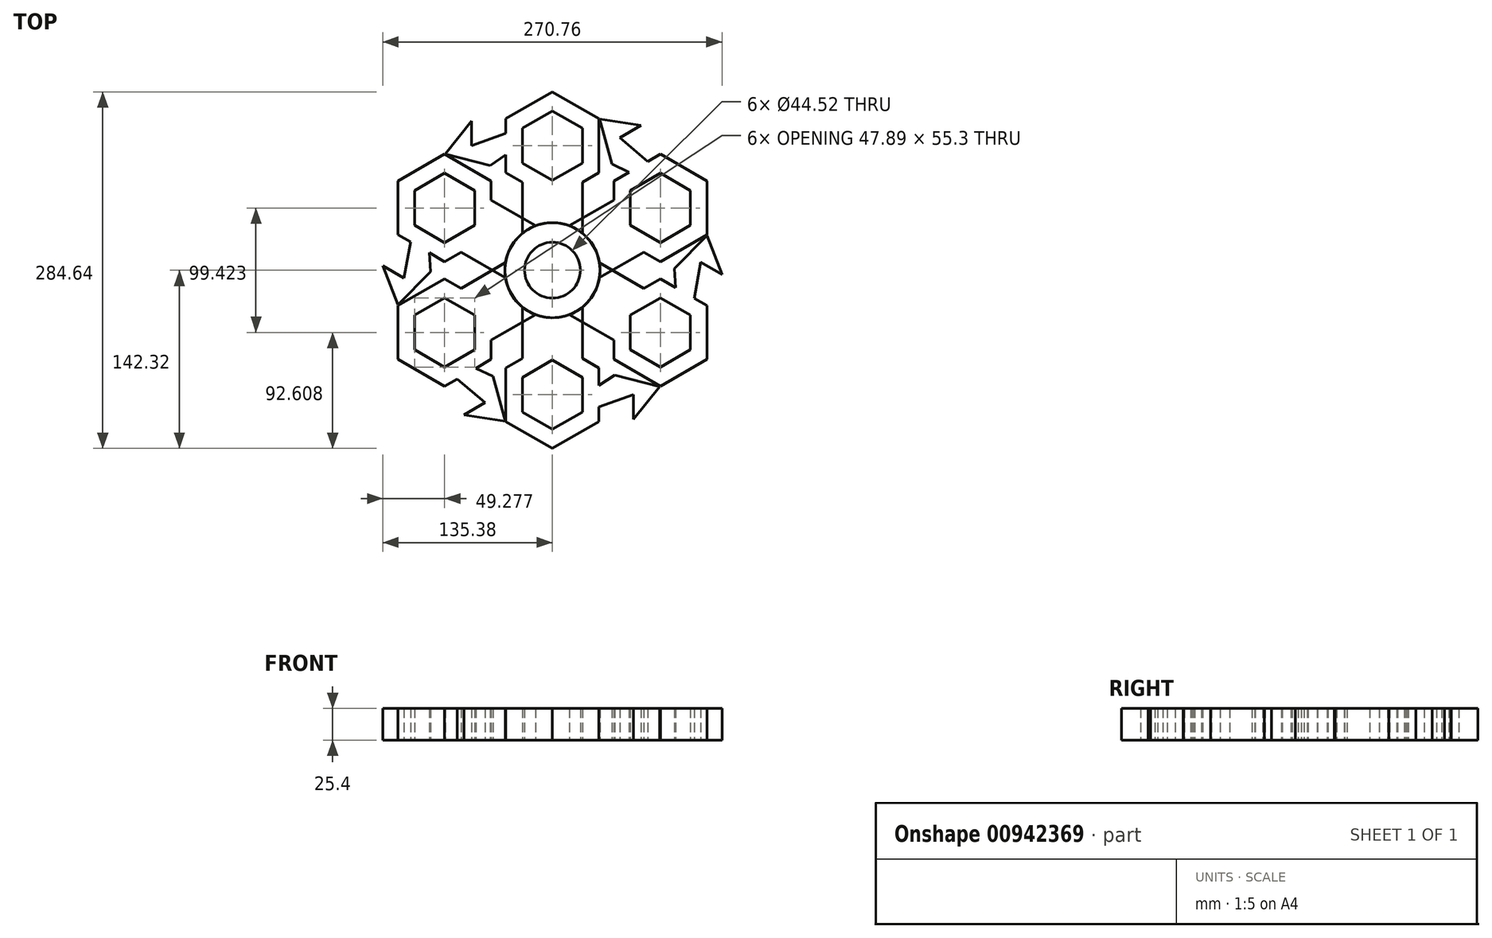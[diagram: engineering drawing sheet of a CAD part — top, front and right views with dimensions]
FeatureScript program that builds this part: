
annotation { "Feature Type Name" : "Feature", "Feature Type Description" : "" }
export const myFeature = defineFeature(function(context is Context, id is Id, definition is map)
    precondition{}
    {
        {
            var Q0;
            Q0=qCreatedBy(makeId("Top.planeOp"),FACE);
            var sketch = newSketch(context, id + "F0", { "sketchPlane" : qUnion([Q0])});
            skCircle(sketch, "E0", {"center": v(0, 0) * mm, "radius": 22.26 * mm});
            skCircle(sketch, "E1", {"center": v(0, 0) * mm, "radius": 37.94 * mm});
            skLineSegment(sketch, "E2", {"start": v(0, 0) * mm, "end": v(0, 93.5) * mm});
            skLineSegment(sketch, "E3", {"start": v(23.94, 29.43) * mm, "end": v(23.94, 85.6) * mm});
            skCircle(sketch, "E4.cCircle", {"center": v(0, 99.42) * mm, "radius": 23.94 * mm, "construction": true});
            skLineSegment(sketch, "E4.0", {"start": v(0, 127.07) * mm, "end": v(23.94, 113.25) * mm});
            skLineSegment(sketch, "E4.1", {"start": v(23.94, 113.25) * mm, "end": v(23.94, 85.6) * mm});
            skLineSegment(sketch, "E4.2", {"start": v(23.94, 85.6) * mm, "end": v(0, 71.77) * mm});
            skLineSegment(sketch, "E4.3", {"start": v(0, 71.77) * mm, "end": v(-23.94, 85.6) * mm});
            skLineSegment(sketch, "E4.4", {"start": v(-23.94, 85.6) * mm, "end": v(-23.94, 113.25) * mm});
            skLineSegment(sketch, "E4.5", {"start": v(-23.94, 113.25) * mm, "end": v(0, 127.07) * mm});
            skPoint(sketch, "E4.0.midPoint", {"position": v(11.97, 120.16) * mm});
            skLineSegment(sketch, "E5.1.0", {"start": v(-86.1, 22.06) * mm, "end": v(-110.05, 35.89) * mm});
            skLineSegment(sketch, "E5.1.1", {"start": v(-110.05, 35.89) * mm, "end": v(-110.05, 63.54) * mm});
            skLineSegment(sketch, "E5.1.2", {"start": v(-110.05, 63.54) * mm, "end": v(-86.1, 77.36) * mm});
            skLineSegment(sketch, "E5.1.3", {"start": v(-86.1, 77.36) * mm, "end": v(-62.16, 63.54) * mm});
            skLineSegment(sketch, "E5.1.4", {"start": v(-62.16, 63.54) * mm, "end": v(-62.16, 35.89) * mm});
            skLineSegment(sketch, "E5.1.5", {"start": v(-62.16, 35.89) * mm, "end": v(-86.1, 22.06) * mm});
            skLineSegment(sketch, "E5.2.0", {"start": v(-62.16, -63.54) * mm, "end": v(-86.1, -77.36) * mm});
            skLineSegment(sketch, "E5.2.1", {"start": v(-86.1, -77.36) * mm, "end": v(-110.05, -63.54) * mm});
            skLineSegment(sketch, "E5.2.2", {"start": v(-110.05, -63.54) * mm, "end": v(-110.05, -35.89) * mm});
            skLineSegment(sketch, "E5.2.3", {"start": v(-110.05, -35.89) * mm, "end": v(-86.1, -22.06) * mm});
            skLineSegment(sketch, "E5.2.4", {"start": v(-86.1, -22.06) * mm, "end": v(-62.16, -35.89) * mm});
            skLineSegment(sketch, "E5.2.5", {"start": v(-62.16, -35.89) * mm, "end": v(-62.16, -63.54) * mm});
            skLineSegment(sketch, "E5.3.0", {"start": v(23.94, -85.6) * mm, "end": v(23.94, -113.25) * mm});
            skLineSegment(sketch, "E5.3.1", {"start": v(23.94, -113.25) * mm, "end": v(0, -127.07) * mm});
            skLineSegment(sketch, "E5.3.2", {"start": v(0, -127.07) * mm, "end": v(-23.94, -113.25) * mm});
            skLineSegment(sketch, "E5.3.3", {"start": v(-23.94, -113.25) * mm, "end": v(-23.94, -85.6) * mm});
            skLineSegment(sketch, "E5.3.4", {"start": v(-23.94, -85.6) * mm, "end": v(0, -71.77) * mm});
            skLineSegment(sketch, "E5.3.5", {"start": v(0, -71.77) * mm, "end": v(23.94, -85.6) * mm});
            skLineSegment(sketch, "E5.4.0", {"start": v(86.1, -22.06) * mm, "end": v(110.05, -35.89) * mm});
            skLineSegment(sketch, "E5.4.1", {"start": v(110.05, -35.89) * mm, "end": v(110.05, -63.54) * mm});
            skLineSegment(sketch, "E5.4.2", {"start": v(110.05, -63.54) * mm, "end": v(86.1, -77.36) * mm});
            skLineSegment(sketch, "E5.4.3", {"start": v(86.1, -77.36) * mm, "end": v(62.16, -63.54) * mm});
            skLineSegment(sketch, "E5.4.4", {"start": v(62.16, -63.54) * mm, "end": v(62.16, -35.89) * mm});
            skLineSegment(sketch, "E5.4.5", {"start": v(62.16, -35.89) * mm, "end": v(86.1, -22.06) * mm});
            skLineSegment(sketch, "E5.5.0", {"start": v(62.16, 63.54) * mm, "end": v(86.1, 77.36) * mm});
            skLineSegment(sketch, "E5.5.1", {"start": v(86.1, 77.36) * mm, "end": v(110.05, 63.54) * mm});
            skLineSegment(sketch, "E5.5.2", {"start": v(110.05, 63.54) * mm, "end": v(110.05, 35.89) * mm});
            skLineSegment(sketch, "E5.5.3", {"start": v(110.05, 35.89) * mm, "end": v(86.1, 22.06) * mm});
            skLineSegment(sketch, "E5.5.4", {"start": v(86.1, 22.06) * mm, "end": v(62.16, 35.89) * mm});
            skLineSegment(sketch, "E5.5.5", {"start": v(62.16, 35.89) * mm, "end": v(62.16, 63.54) * mm});
            skLineSegment(sketch, "E6.MirrorCS", {"start": v(-23.94, 29.43) * mm, "end": v(-23.94, 85.6) * mm});
            skLineSegment(sketch, "E7.0", {"start": v(-37.15, 77.97) * mm, "end": v(-37.15, 120.87) * mm});
            skLineSegment(sketch, "E7.1", {"start": v(0, 142.32) * mm, "end": v(37.15, 120.87) * mm});
            skLineSegment(sketch, "E7.2", {"start": v(37.15, 120.87) * mm, "end": v(37.15, 77.97) * mm});
            skLineSegment(sketch, "E7.3", {"start": v(-37.15, 120.87) * mm, "end": v(0, 142.32) * mm});
            skLineSegment(sketch, "E7.4", {"start": v(37.15, 77.97) * mm, "end": v(0, 56.52) * mm});
            skLineSegment(sketch, "E7.5", {"start": v(0, 56.52) * mm, "end": v(-37.15, 77.97) * mm});
            skLineSegment(sketch, "E8", {"start": v(-37.15, 109.33) * mm, "end": v(-64.66, 99.42) * mm});
            skPoint(sketch, "E8.endSnap0", {"position": v(-37.15, 99.42) * mm});
            skLineSegment(sketch, "E9", {"start": v(-64.66, 99.42) * mm, "end": v(-64.66, 119) * mm});
            skLineSegment(sketch, "E10", {"start": v(-64.66, 119) * mm, "end": v(-85.6, 92.85) * mm});
            skLineSegment(sketch, "E11", {"start": v(-85.6, 92.85) * mm, "end": v(-49.68, 83.63) * mm});
            skLineSegment(sketch, "E12", {"start": v(-49.68, 83.63) * mm, "end": v(-37.15, 92.11) * mm});
            skSolve(sketch);
        }
        {
            var Q0;
            Q0=makeQuery(id+"F0.imprint","IMPRINT",FACE,{"disambiguationData":[TD([[makeQuery(id+"F0.imprint","IMPRINT",EDGE,{"derivedFrom":sQuery(id+"F0.wireOp",EDGE,"E4.0")}),1.0]])]});
            var Q1;
            {var subQ0=sQuery(id+"F0.wireOp",EDGE,"E4.3");Q1=makeQuery(id+"F0.imprint","IMPRINT",FACE,{"disambiguationData":[TD([[makeQuery(id+"F0.imprint","IMPRINT",EDGE,{"derivedFrom":subQ0}),1.0]])]});}
            var Q2;
            {var subQ0=sQuery(id+"F0.wireOp",EDGE,"E4.2");Q2=makeQuery(id+"F0.imprint","IMPRINT",FACE,{"disambiguationData":[TD([[makeQuery(id+"F0.imprint","IMPRINT",EDGE,{"derivedFrom":subQ0}),1.0]])]});}
            var Q3;
            {var subQ0=sQuery(id+"F0.wireOp",EDGE,"E3");var subQ1=sQuery(id+"F0.wireOp",EDGE,"E1");var subQ2=makeQuery(id+"F0.imprint","INTERSECT",VERTEX,{"derivedFrom":[subQ1,subQ0]});Q3=makeQuery(id+"F0.imprint","IMPRINT",FACE,{"disambiguationData":[TD([[makeQuery(id+"F0.imprint","IMPRINT",EDGE,{"disambiguationData":[TD([[subQ2,-1.0]])],"derivedFrom":subQ1}),-1.0]])]});}
            var Q4;
            {var subQ0=sQuery(id+"F0.wireOp",EDGE,"E6.MirrorCS");var subQ1=sQuery(id+"F0.wireOp",EDGE,"E1");var subQ2=makeQuery(id+"F0.imprint","INTERSECT",VERTEX,{"derivedFrom":[subQ1,subQ0]});Q4=makeQuery(id+"F0.imprint","IMPRINT",FACE,{"disambiguationData":[TD([[makeQuery(id+"F0.imprint","IMPRINT",EDGE,{"disambiguationData":[TD([[subQ2,1.0]])],"derivedFrom":subQ1}),-1.0]])]});}
            var Q5;
            Q5=makeQuery(id+"F0.imprint","IMPRINT",FACE,{"disambiguationData":[TD([[makeQuery(id+"F0.imprint","IMPRINT",EDGE,{"derivedFrom":sQuery(id+"F0.wireOp",EDGE,"E0")}),-1.0]])]});
            var Q6;
            {var subQ0=sQuery(id+"F0.wireOp",EDGE,"E8");Q6=makeQuery(id+"F0.imprint","IMPRINT",FACE,{"disambiguationData":[TD([[makeQuery(id+"F0.imprint","IMPRINT",EDGE,{"derivedFrom":subQ0}),1.0]])]});}
            var Q7;
            Q7=makeQuery(id+"F0.imprint","IMPRINT",FACE,{"disambiguationData":[TD([[makeQuery(id+"F0.imprint","IMPRINT",EDGE,{"derivedFrom":sQuery(id+"F0.wireOp",EDGE,"E5.1.0")}),-1.0]])]});
            extrude(context, id + "F1", {"entities" : qUnion([Q0, Q1, Q2, Q3, Q4, Q5, Q6, Q7]), "depth" : 25.4 * mm, "offsetDistance" : 25.4 * mm});
        }
        {
            var Q0;
            Q0=qCreatedBy(makeId("Right.planeOp"),FACE);
            var sketch = newSketch(context, id + "F2", { "sketchPlane" : qUnion([Q0])});
            skLineSegment(sketch, "E13", {"start": v(0, 0) * mm, "end": v(0, 59.92) * mm});
            skSolve(sketch);
        }
        {
            var Q0;
            Q0=makeQuery(id+"F1.opExtrude","SWEPT_BODY",BODY,{"disambiguationData":[OSD([sQuery(id+"F0.wireOp",EDGE,"E0"),sQuery(id+"F0.wireOp",EDGE,"E1"),sQuery(id+"F0.wireOp",EDGE,"E3"),sQuery(id+"F0.wireOp",EDGE,"E4.0"),sQuery(id+"F0.wireOp",EDGE,"E4.1"),sQuery(id+"F0.wireOp",EDGE,"E4.2"),sQuery(id+"F0.wireOp",EDGE,"E4.3"),sQuery(id+"F0.wireOp",EDGE,"E4.4"),sQuery(id+"F0.wireOp",EDGE,"E4.5"),sQuery(id+"F0.wireOp",EDGE,"E6.MirrorCS"),sQuery(id+"F0.wireOp",EDGE,"E7.0"),sQuery(id+"F0.wireOp",EDGE,"E7.1"),sQuery(id+"F0.wireOp",EDGE,"E7.2"),sQuery(id+"F0.wireOp",EDGE,"E7.3"),sQuery(id+"F0.wireOp",EDGE,"E7.4"),sQuery(id+"F0.wireOp",EDGE,"E7.5")])]});
            var Q1;
            Q1=sQuery(id+"F2.wireOp",EDGE,"E13");
            circularPattern(context, id + "F3", {"entities" : qUnion([Q0]), "axis" : qUnion([Q1]), "angle" : 360 * degree, "instanceCount" : 6, "equalSpace" : true});
        }
    });
